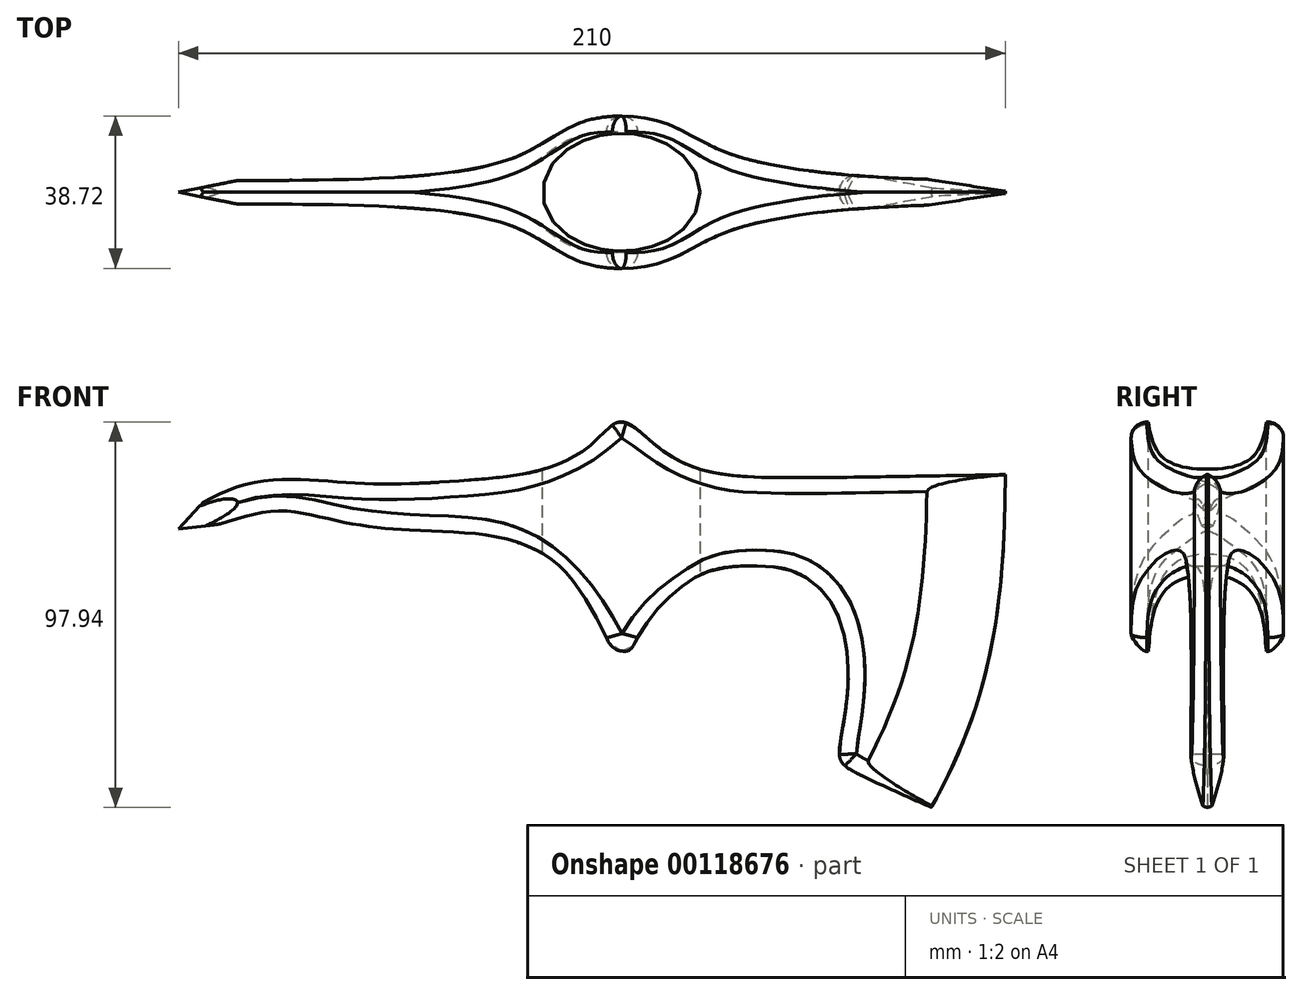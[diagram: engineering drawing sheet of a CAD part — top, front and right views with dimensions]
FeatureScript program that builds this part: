
annotation { "Feature Type Name" : "Feature", "Feature Type Description" : "" }
export const myFeature = defineFeature(function(context is Context, id is Id, definition is map)
    precondition{}
    {
        {
            var Q0;
            Q0=qCreatedBy(makeId("Top.planeOp"),FACE);
            var sketch = newSketch(context, id + "F0", { "sketchPlane" : qUnion([Q0])});
            skLineSegment(sketch, "E0", {"start": v(-160.46, 0) * mm, "end": v(161.68, 0) * mm, "construction": true});
            skPoint(sketch, "E1", {"position": v(-112.5, 0) * mm});
            skPoint(sketch, "E2", {"position": v(97.5, 0) * mm});
            skPoint(sketch, "E3", {"position": v(20, 0) * mm});
            skPoint(sketch, "E4", {"position": v(0, 15) * mm});
            skEllipse(sketch, "E5", {"center": v(0, 0) * mm, "majorRadius": 20 * mm, "minorRadius": 15 * mm, "majorAxis": v(1, 0)});
            skLineSegment(sketch, "E6", {"start": v(0, 15) * mm, "end": v(0, 0) * mm, "construction": true});
            skLineSegment(sketch, "E7", {"start": v(-20, 0) * mm, "end": v(0, 0) * mm, "construction": true});
            skLineSegment(sketch, "E8", {"start": v(0, 0) * mm, "end": v(20, 0) * mm, "construction": true});
            skPoint(sketch, "E9", {"position": v(-97.5, 0) * mm});
            skPoint(sketch, "E10", {"position": v(-97.5, 3) * mm});
            skLineSegment(sketch, "E11", {"start": v(-112.5, 0) * mm, "end": v(-97.5, 3) * mm});
            skPoint(sketch, "E12", {"position": v(-27.5, 0) * mm});
            skPoint(sketch, "E13", {"position": v(27.5, 0) * mm});
            skPoint(sketch, "E14.1.internal.snap0", {"position": v(0, 7.5) * mm});
            skPoint(sketch, "E14.2.internal.snap0", {"position": v(-10, 0) * mm});
            skPoint(sketch, "E14.3.internal.snap0", {"position": v(10, 0) * mm});
            skPoint(sketch, "E14.4.internal.snap0", {"position": v(0, 7.5) * mm});
            skFitSpline(sketch, "E14", {"points": [v(-97.5, 3) * mm, v(-27.5, 8.7) * mm, v(-10, 17.83) * mm, v(10, 17.91) * mm, v(27.5, 9.8) * mm, v(97.5, 3) * mm], "startDerivative": vector(335.73, 0) * mm, "endDerivative": vector(321.52, 0) * mm});
            skLineSegment(sketch, "E15", {"start": v(97.5, 3) * mm, "end": v(97.5, 0) * mm});
            skLineSegment(sketch, "E16.MirrorCS", {"start": v(-112.5, 0) * mm, "end": v(-97.5, -3) * mm});
            skFitSpline(sketch, "E17.MirrorCS", {"points": [v(-97.5, -3) * mm, v(-27.5, -8.7) * mm, v(-10, -17.83) * mm, v(10, -17.91) * mm, v(27.5, -9.8) * mm, v(97.5, -3) * mm], "startDerivative": vector(335.73, 0) * mm, "endDerivative": vector(321.52, 0) * mm});
            skLineSegment(sketch, "E18.MirrorCS", {"start": v(97.5, -3) * mm, "end": v(97.5, 0) * mm});
            skSolve(sketch);
        }
        {
            var Q0;
            Q0=makeQuery(id+"F0.imprint","IMPRINT",FACE,{"disambiguationData":[TD([[makeQuery(id+"F0.imprint","IMPRINT",EDGE,{"derivedFrom":sQuery(id+"F0.wireOp",EDGE,"E5")}),-1.0]])]});
            extrude(context, id + "F1", {"entities" : qUnion([Q0]), "depth" : 105 * mm});
        }
        {
            var Q0;
            Q0=makeQuery(id+"F1.opExtrude","SWEPT_EDGE",EDGE,{"disambiguationData":[OSD([sQuery(id+"F0.wireOp",EDGE,"E14"),sQuery(id+"F0.wireOp",EDGE,"E15")])]});
            cPlane(context, id + "F2", {"entities" : qUnion([Q0]), "cplaneType" : CPlaneType.LINE_ANGLE, "offset" : 25 * mm, "angle" : 270 * degree, "width" : 150 * mm, "height" : 150 * mm});
        }
        {
            var Q0;
            Q0=qCreatedBy(id+"F2.planeOp",FACE);
            var sketch = newSketch(context, id + "F3", { "sketchPlane" : qUnion([Q0])});
            skLineSegment(sketch, "E19", {"start": v(0, 0) * mm, "end": v(0, 119.81) * mm, "construction": true});
            skLineSegment(sketch, "E20.0", {"start": v(97.5, 105) * mm, "end": v(97.5, 0) * mm, "construction": true});
            skLineSegment(sketch, "E21.0", {"start": v(-112.5, 105) * mm, "end": v(-112.5, 0) * mm, "construction": true});
            skFitSpline(sketch, "E22.0", {"points": [v(-97.5, 105) * mm, v(-66.1, 105) * mm, v(-28.71, 105) * mm, v(-11.43, 105) * mm, v(11.36, 105) * mm, v(28.65, 105) * mm, v(67.4, 105) * mm, v(97.5, 105) * mm], "construction": true});
            skFitSpline(sketch, "E23.0", {"points": [v(-97.5, 0) * mm, v(-66.1, 0) * mm, v(-28.71, 0) * mm, v(-11.43, 0) * mm, v(11.36, 0) * mm, v(28.65, 0) * mm, v(67.4, 0) * mm, v(97.5, 0) * mm], "construction": true});
            skLineSegment(sketch, "E24", {"start": v(97.5, 91.06) * mm, "end": v(-112.5, 91.06) * mm, "construction": true});
            skFitSpline(sketch, "E25", {"points": [v(97.5, 91.06) * mm, v(46, 90.12) * mm, v(21.77, 91.78) * mm, v(10.06, 97.33) * mm, v(2.48, 103.46) * mm, v(0, 104.26) * mm, v(-2.16, 103.6) * mm, v(-8.46, 97.87) * mm, v(-19.6, 92.33) * mm, v(-32.86, 90.01) * mm, v(-60.94, 88.55) * mm, v(-78, 89.6) * mm, v(-87.84, 89.7) * mm, v(-95.02, 88.67) * mm, v(-100.88, 86.62) * mm, v(-106, 84.13) * mm], "startDerivative": vector(-404.28, -9.77) * mm, "endDerivative": vector(-110.15, -56.2) * mm});
            skLineSegment(sketch, "E26", {"start": v(-106, 84.13) * mm, "end": v(-112.5, 77.1) * mm});
            skLineSegment(sketch, "E27", {"start": v(-112.5, 77.1) * mm, "end": v(-101.32, 78.41) * mm});
            skFitSpline(sketch, "E28", {"points": [v(-101.32, 78.41) * mm, v(-93.55, 80.6) * mm, v(-85.05, 81.49) * mm, v(-71.94, 79.02) * mm, v(-58.23, 77.1) * mm, v(-40.1, 76.13) * mm, v(-31.05, 74.97) * mm, v(-22.59, 72.2) * mm, v(-14.56, 66.5) * mm, v(-6.68, 55.12) * mm, v(-3.91, 49.58) * mm, v(-1.72, 46.66) * mm, v(1.78, 46.22) * mm, v(3.96, 49.27) * mm, v(9.68, 57.36) * mm, v(15.87, 62.84) * mm, v(23.25, 66.65) * mm, v(36.35, 67.6) * mm, v(44.69, 65.94) * mm, v(51.12, 61.17) * mm, v(55.64, 53.31) * mm, v(57.55, 37.12) * mm, v(55.47, 21.76) * mm, v(56, 17.8) * mm, v(61.16, 14.36) * mm, v(78.72, 6.26) * mm], "startDerivative": vector(209.45, 63.97) * mm, "endDerivative": vector(343.39, -154.84) * mm});
            skFitSpline(sketch, "E29", {"points": [v(78.72, 6.26) * mm, v(97.5, 91.06) * mm], "startDerivative": vector(43.4, 78.52) * mm, "endDerivative": vector(0, 108.2) * mm});
            skLineSegment(sketch, "E30.bottom", {"start": v(-118.55, 109.7) * mm, "end": v(108.37, 109.7) * mm});
            skLineSegment(sketch, "E30.top", {"start": v(-118.55, -5.86) * mm, "end": v(108.37, -5.86) * mm});
            skLineSegment(sketch, "E30.left", {"start": v(-118.55, 109.7) * mm, "end": v(-118.55, -5.86) * mm});
            skLineSegment(sketch, "E30.right", {"start": v(108.37, 109.7) * mm, "end": v(108.37, -5.86) * mm});
            skSolve(sketch);
        }
        {
            var Q0;
            Q0=makeQuery(id+"F3.imprint","IMPRINT",FACE,{"disambiguationData":[TD([[makeQuery(id+"F3.imprint","IMPRINT",EDGE,{"derivedFrom":sQuery(id+"F3.wireOp",EDGE,"E25")}),-1.0]])]});
            extrude(context, id + "F4", {"entities" : qUnion([Q0]), "operationType" : NewBodyOperationType.REMOVE, "oppositeDirection" : true, "depth" : 100 * mm, "symmetric" : true});
        }
        {
            var Q0;
            Q0=makeQuery(id+"F4.boolean.opBoolean","INTERSECT",EDGE,{"derivedFrom":[makeQuery(id+"F1.opExtrude","SWEPT_FACE",FACE,{"disambiguationData":[OSD([sQuery(id+"F0.wireOp",EDGE,"E14")])]}),makeQuery(id+"F4.opExtrude","SWEPT_FACE",FACE,{"disambiguationData":[OSD([sQuery(id+"F3.wireOp",EDGE,"E29")])]})]});
            var Q1;
            Q1=makeQuery(id+"F4.boolean.opBoolean","INTERSECT",EDGE,{"derivedFrom":[makeQuery(id+"F1.opExtrude","SWEPT_FACE",FACE,{"disambiguationData":[OSD([sQuery(id+"F0.wireOp",EDGE,"E17.MirrorCS")])]}),makeQuery(id+"F4.opExtrude","SWEPT_FACE",FACE,{"disambiguationData":[OSD([sQuery(id+"F3.wireOp",EDGE,"E29")])]})]});
            chamfer(context, id + "F5", {"entities" : qUnion([Q0, Q1]), "chamferType" : ChamferType.TWO_OFFSETS, "width1" : 20 * mm, "oppositeDirection" : false, "width2" : 3 * mm, "tangentPropagation" : true});
        }
        {
            var Q0;
            Q0=makeQuery(id+"F4.boolean.opBoolean","INTERSECT",EDGE,{"derivedFrom":[makeQuery(id+"F1.opExtrude","SWEPT_FACE",FACE,{"disambiguationData":[OSD([sQuery(id+"F0.wireOp",EDGE,"E14")])]}),makeQuery(id+"F4.opExtrude","SWEPT_FACE",FACE,{"disambiguationData":[OSD([sQuery(id+"F3.wireOp",EDGE,"E25")])]})]});
            var Q1;
            Q1=makeQuery(id+"F4.boolean.opBoolean","INTERSECT",EDGE,{"derivedFrom":[makeQuery(id+"F1.opExtrude","SWEPT_FACE",FACE,{"disambiguationData":[OSD([sQuery(id+"F0.wireOp",EDGE,"E17.MirrorCS")])]}),makeQuery(id+"F4.opExtrude","SWEPT_FACE",FACE,{"disambiguationData":[OSD([sQuery(id+"F3.wireOp",EDGE,"E25")])]})]});
            var Q2;
            Q2=makeQuery(id+"F4.boolean.opBoolean","INTERSECT",EDGE,{"derivedFrom":[makeQuery(id+"F1.opExtrude","SWEPT_FACE",FACE,{"disambiguationData":[OSD([sQuery(id+"F0.wireOp",EDGE,"E14")])]}),makeQuery(id+"F4.opExtrude","SWEPT_FACE",FACE,{"disambiguationData":[OSD([sQuery(id+"F3.wireOp",EDGE,"E28")])]})]});
            var Q3;
            Q3=makeQuery(id+"F4.boolean.opBoolean","INTERSECT",EDGE,{"derivedFrom":[makeQuery(id+"F1.opExtrude","SWEPT_FACE",FACE,{"disambiguationData":[OSD([sQuery(id+"F0.wireOp",EDGE,"E17.MirrorCS")])]}),makeQuery(id+"F4.opExtrude","SWEPT_FACE",FACE,{"disambiguationData":[OSD([sQuery(id+"F3.wireOp",EDGE,"E28")])]})]});
            fillet(context, id + "F6", {"entities" : qUnion([Q0, Q1, Q2, Q3]), "radius" : 4 * mm, "tangentPropagation" : true, "allowEdgeOverflow" : false});
        }
    });
